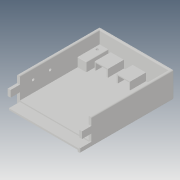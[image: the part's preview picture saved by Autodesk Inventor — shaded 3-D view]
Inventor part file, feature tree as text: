
AUTODESK INVENTOR PART (.ipt)
format: ipt  version: 2019 (Build 230136000, 136)  size: 403,968 bytes
history: native  units: mm
features: extrude x10, sketch x10, projected_geometry x5, other x4, fillet x2, plane x2, surface_op x1
ambient origin geometry x8: Origin, YZ Plane, XZ Plane, XY Plane, X Axis, Y Axis, Z Axis, Center Point
bodies: Solid1 (feature_tree)
feature tree (34):
  extrude  "Extrusion1"  Depth=170.0mm
  extrude  "Extrusion2"  Depth=5.0mm
  extrude  "Extrusion3"  Depth=25.0mm TaperAngle=0.0deg
  fillet  "Fillet1"  Radius=2.0mm
  extrude  "Extrusion4"  TaperAngle=0.0deg  [1 undecoded]
  extrude  "Extrusion5"  Depth=40.0mm
  fillet  "Fillet2"  [1 undecoded]
  plane  "Work Plane2"
  extrude  "Extrusion7"  Depth=35.0mm
  plane  "Work Plane1"
  extrude  "Extrusion8"  Depth=16.0mm TaperAngle=0.0deg
  surface_op  "Sculpt3"
  sketch  "Sketch8"  dims[d20=4.5mm d22=6.0mm]
  extrude  "Extrusion15"  Depth=6.0mm
  extrude  "Extrusion16"  Depth=7.0mm
  extrude  "Extrusion18"  Depth=1.0mm
  sketch  "Sketch1"  dims[d0=135.0mm d1=170.0mm]
  sketch  "Sketch2"  dims[d2=46.7mm d3=0.0mm d4=5.0mm]
  projected_geometry  "Projected Loop1"
  sketch  "Sketch3"  dims[d5=38.7mm d6=0.0mm d7=25.0mm d8=0.0mm d9=2.0mm]
  projected_geometry  "Projected Loop2"
  sketch  "Sketch4"  dims[d10=0.0mm d11=0.0mm]
  sketch  "Sketch5"  dims[d12=16.0mm d13=40.0mm d14=0.0mm]
  sketch  "Sketch6"  dims[d15=0.0mm d16=35.0mm]
  sketch  "Sketch7"  dims[d17=16.0mm d18=16.0mm d19=0.0mm]
  sketch  "Sketch14"  dims[d23=4.5mm d24=7.0mm]
  projected_geometry  "Projected Loop10"
  sketch  "Sketch16"  dims[d26=12.0mm d27=0.0mm d28=1.0mm d29=4.5mm d30=4.5mm d31=30.8mm d34=90.0mm d37=0.0mm d38=0.0mm d39=-1.5mm d40=7.5mm d41=7.5mm d42=3.15mm d43=0.0mm d44=10.0mm d45=12.5mm d46=18.0mm d51=20.0mm d70=1.75mm d91=12.0mm d92=8.0mm d93=2.05mm d94=2.05mm d95=20.0mm d96=29.0mm d97=0.0mm d98=0.8mm d99=0.8mm d100=1.8mm d101=4.4mm d102=0.0mm d105=1.8mm d106=4.4mm d107=0.0mm]
  projected_geometry  "Projected Loop13"
  projected_geometry  "Projected Loop14"
  other  "Composite3"
  other  "Srf3"
  other  "Assembly1"
  other  "Case_B1:1"
note: 2 required parameter values undecoded (feature->parameter linkage not recoverable at this tier; creation-order binding heuristic only, values carry confidence <= 0.55)
